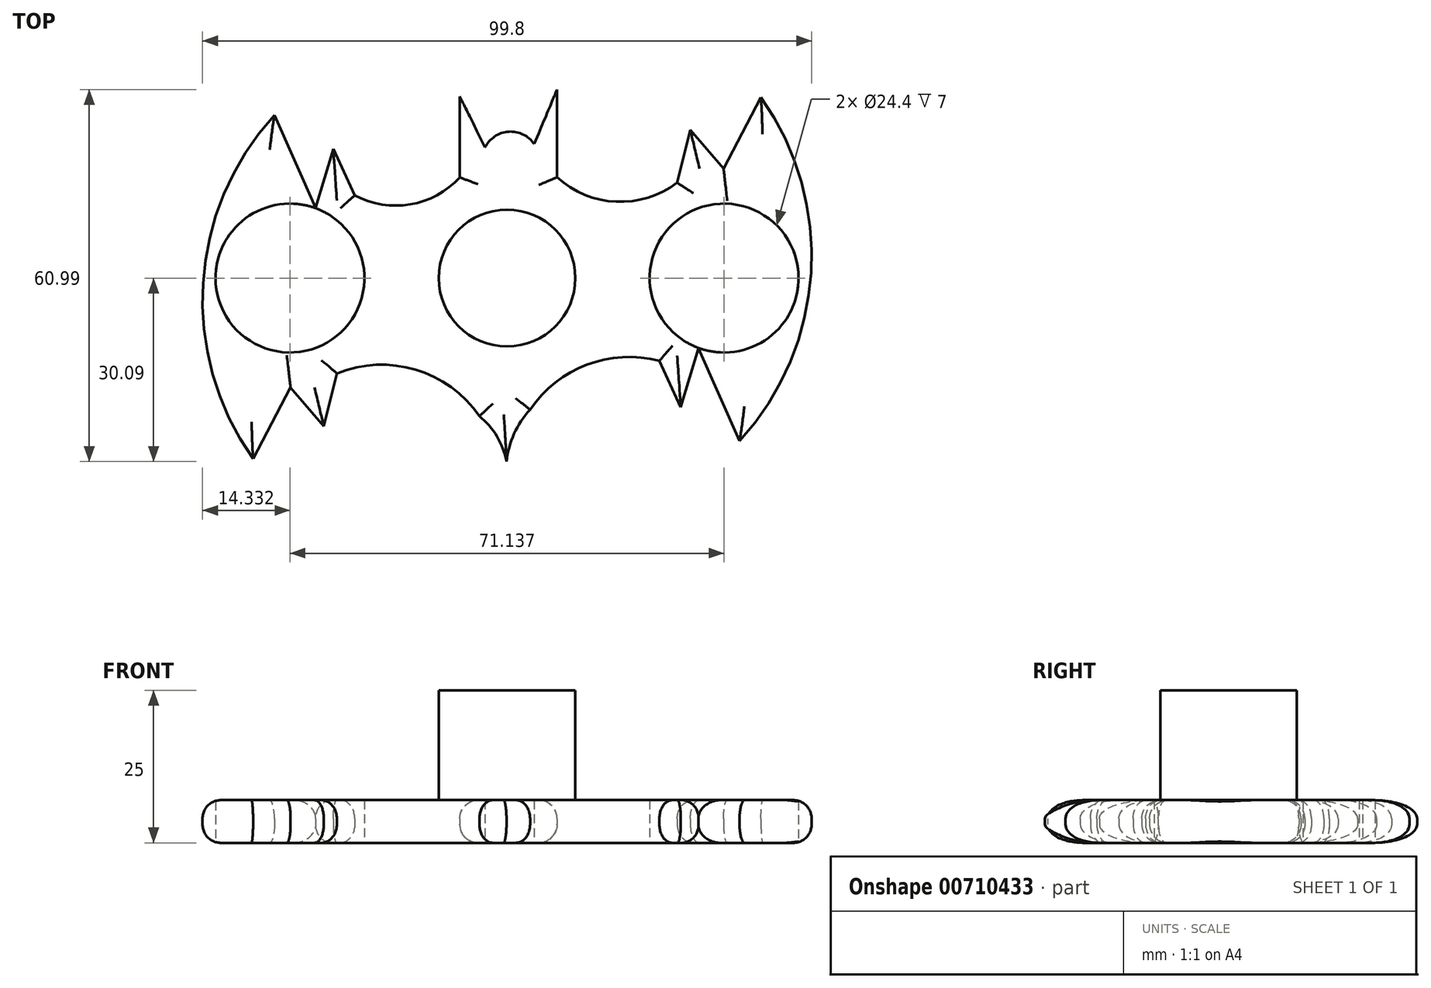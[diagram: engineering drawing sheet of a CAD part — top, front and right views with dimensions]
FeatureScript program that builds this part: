
annotation { "Feature Type Name" : "Feature", "Feature Type Description" : "" }
export const myFeature = defineFeature(function(context is Context, id is Id, definition is map)
    precondition{}
    {
        {
            var Q0;
            Q0=qCreatedBy(makeId("Top.planeOp"),FACE);
            var sketch = newSketch(context, id + "F0", { "sketchPlane" : qUnion([Q0])});
            skCircle(sketch, "E0", {"center": v(0, 0) * mm, "radius": 11.2 * mm});
            skCircle(sketch, "E1", {"center": v(0, 0) * mm, "radius": 13.2 * mm});
            skArc(sketch, "E2", {"start": v(-38.1, 26.72) * mm, "mid": v(-49.82, -0.84) * mm, "end": v(-41.61, -29.64) * mm});
            skArc(sketch, "E3.1.0", {"start": v(38.1, -26.72) * mm, "mid": v(49.82, 0.84) * mm, "end": v(41.61, 29.64) * mm});
            skLineSegment(sketch, "E4", {"start": v(-41.61, -29.64) * mm, "end": v(-35.48, -17.96) * mm});
            skLineSegment(sketch, "E5", {"start": v(-35.48, -17.96) * mm, "end": v(-35.48, -24.97) * mm});
            skArc(sketch, "E6", {"start": v(-4.53, -22.63) * mm, "mid": v(-14.98, -15.03) * mm, "end": v(-27.89, -15.62) * mm});
            skLineSegment(sketch, "E7.1.0", {"start": v(41.61, 29.64) * mm, "end": v(35.48, 17.96) * mm});
            skLineSegment(sketch, "E7.1.1", {"start": v(35.48, 17.96) * mm, "end": v(30.03, 24.29) * mm});
            skLineSegment(sketch, "E7.1.2", {"start": v(30.03, 24.29) * mm, "end": v(27.89, 15.62) * mm});
            skLineSegment(sketch, "E8", {"start": v(38.1, -26.72) * mm, "end": v(31.4, -11.53) * mm});
            skLineSegment(sketch, "E9", {"start": v(31.4, -11.53) * mm, "end": v(28.47, -21.17) * mm});
            skLineSegment(sketch, "E10", {"start": v(28.47, -21.17) * mm, "end": v(24.97, -13.58) * mm});
            skArc(sketch, "E11.1.0", {"start": v(-24.97, 13.58) * mm, "mid": v(-15.85, 12.08) * mm, "end": v(-7.74, 16.5) * mm});
            skLineSegment(sketch, "E11.1.2", {"start": v(-28.47, 21.17) * mm, "end": v(-24.97, 13.58) * mm});
            skLineSegment(sketch, "E11.1.4", {"start": v(-31.4, 11.53) * mm, "end": v(-28.47, 21.17) * mm});
            skLineSegment(sketch, "E11.1.5", {"start": v(-38.1, 26.72) * mm, "end": v(-31.4, 11.53) * mm});
            skArc(sketch, "E12", {"start": v(0, -34.06) * mm, "mid": v(-0.76, -27.75) * mm, "end": v(-4.53, -22.63) * mm});
            skArc(sketch, "E13.1.0", {"start": v(8.2, 16.53) * mm, "mid": v(17.88, 12.52) * mm, "end": v(27.89, 15.62) * mm});
            skLineSegment(sketch, "E14", {"start": v(-7.74, 16.5) * mm, "end": v(-7.74, 29.75) * mm});
            skLineSegment(sketch, "E15", {"start": v(-7.74, 29.75) * mm, "end": v(-3.6, 21.41) * mm});
            skLineSegment(sketch, "E16", {"start": v(8.2, 16.53) * mm, "end": v(8.2, 30.9) * mm});
            skLineSegment(sketch, "E17", {"start": v(8.2, 30.9) * mm, "end": v(4.45, 21.97) * mm});
            skArc(sketch, "E18", {"start": v(4.45, 21.97) * mm, "mid": v(0.27, 24) * mm, "end": v(-3.6, 21.41) * mm});
            skArc(sketch, "E19", {"start": v(24.97, -13.58) * mm, "mid": v(13.1, -14.2) * mm, "end": v(3.78, -21.57) * mm});
            skArc(sketch, "E20", {"start": v(3.78, -21.57) * mm, "mid": v(0.47, -27.38) * mm, "end": v(0, -34.06) * mm});
            skLineSegment(sketch, "E21.1.0", {"start": v(-35.48, -17.96) * mm, "end": v(-30.03, -24.29) * mm});
            skLineSegment(sketch, "E21.1.1", {"start": v(-30.03, -24.29) * mm, "end": v(-27.89, -15.62) * mm});
            skCircle(sketch, "E22", {"center": v(35.57, 0) * mm, "radius": 12.2 * mm});
            skCircle(sketch, "E23", {"center": v(-35.57, 0) * mm, "radius": 12.2 * mm});
            skSolve(sketch);
        }
        {
            var Q0;
            Q0=makeQuery(id+"F0.imprint","IMPRINT",FACE,{"disambiguationData":[TD([[makeQuery(id+"F0.imprint","IMPRINT",EDGE,{"derivedFrom":sQuery(id+"F0.wireOp",EDGE,"E0")}),-1.0]])]});
            var Q1;
            Q1=makeQuery(id+"F0.imprint","IMPRINT",FACE,{"disambiguationData":[TD([[makeQuery(id+"F0.imprint","IMPRINT",EDGE,{"derivedFrom":sQuery(id+"F0.wireOp",EDGE,"E1")}),-1.0]])]});
            extrude(context, id + "F1", {"entities" : qUnion([Q0, Q1]), "depth" : 7 * mm, "offsetDistance" : 25 * mm});
        }
        {
            var Q0;
            Q0=makeQuery(id+"F1.opExtrude","CAP_EDGE",EDGE,{"disambiguationData":[OSD([sQuery(id+"F0.wireOp",EDGE,"E20")])],"isStart":false});
            var Q1;
            Q1=makeQuery(id+"F1.opExtrude","CAP_EDGE",EDGE,{"disambiguationData":[OSD([sQuery(id+"F0.wireOp",EDGE,"E19")])],"isStart":false});
            var Q2;
            Q2=makeQuery(id+"F1.opExtrude","CAP_EDGE",EDGE,{"disambiguationData":[OSD([sQuery(id+"F0.wireOp",EDGE,"E9")])],"isStart":false});
            var Q3;
            Q3=makeQuery(id+"F1.opExtrude","CAP_EDGE",EDGE,{"disambiguationData":[OSD([sQuery(id+"F0.wireOp",EDGE,"E3.1.0")])],"isStart":false});
            var Q4;
            Q4=makeQuery(id+"F1.opExtrude","CAP_EDGE",EDGE,{"disambiguationData":[OSD([sQuery(id+"F0.wireOp",EDGE,"E8")])],"isStart":false});
            var Q5;
            Q5=makeQuery(id+"F1.opExtrude","CAP_EDGE",EDGE,{"disambiguationData":[OSD([sQuery(id+"F0.wireOp",EDGE,"E7.1.0")])],"isStart":false});
            var Q6;
            Q6=makeQuery(id+"F1.opExtrude","CAP_EDGE",EDGE,{"disambiguationData":[OSD([sQuery(id+"F0.wireOp",EDGE,"E7.1.1")])],"isStart":false});
            var Q7;
            Q7=makeQuery(id+"F1.opExtrude","CAP_EDGE",EDGE,{"disambiguationData":[OSD([sQuery(id+"F0.wireOp",EDGE,"E7.1.2")])],"isStart":false});
            var Q8;
            Q8=makeQuery(id+"F1.opExtrude","CAP_EDGE",EDGE,{"disambiguationData":[OSD([sQuery(id+"F0.wireOp",EDGE,"E13.1.0")])],"isStart":false});
            var Q9;
            Q9=makeQuery(id+"F1.opExtrude","CAP_EDGE",EDGE,{"disambiguationData":[OSD([sQuery(id+"F0.wireOp",EDGE,"E16")])],"isStart":false});
            var Q10;
            Q10=makeQuery(id+"F1.opExtrude","CAP_EDGE",EDGE,{"disambiguationData":[OSD([sQuery(id+"F0.wireOp",EDGE,"E14")])],"isStart":false});
            var Q11;
            Q11=makeQuery(id+"F1.opExtrude","CAP_EDGE",EDGE,{"disambiguationData":[OSD([sQuery(id+"F0.wireOp",EDGE,"E11.1.0")])],"isStart":false});
            var Q12;
            Q12=makeQuery(id+"F1.opExtrude","CAP_EDGE",EDGE,{"disambiguationData":[OSD([sQuery(id+"F0.wireOp",EDGE,"E11.1.2")])],"isStart":false});
            var Q13;
            Q13=makeQuery(id+"F1.opExtrude","CAP_EDGE",EDGE,{"disambiguationData":[OSD([sQuery(id+"F0.wireOp",EDGE,"E11.1.5")])],"isStart":false});
            var Q14;
            Q14=makeQuery(id+"F1.opExtrude","CAP_EDGE",EDGE,{"disambiguationData":[OSD([sQuery(id+"F0.wireOp",EDGE,"E11.1.4")])],"isStart":false});
            var Q15;
            Q15=makeQuery(id+"F1.opExtrude","CAP_EDGE",EDGE,{"disambiguationData":[OSD([sQuery(id+"F0.wireOp",EDGE,"E2")])],"isStart":false});
            var Q16;
            Q16=makeQuery(id+"F1.opExtrude","CAP_EDGE",EDGE,{"disambiguationData":[OSD([sQuery(id+"F0.wireOp",EDGE,"E4")])],"isStart":false});
            var Q17;
            Q17=makeQuery(id+"F1.opExtrude","CAP_EDGE",EDGE,{"disambiguationData":[OSD([sQuery(id+"F0.wireOp",EDGE,"wEF84jsq-XExs-cQrN-D3yr-Ib7uIkRzdJAm")])],"isStart":false});
            var Q18;
            Q18=makeQuery(id+"F1.opExtrude","CAP_EDGE",EDGE,{"disambiguationData":[OSD([sQuery(id+"F0.wireOp",EDGE,"E12")])],"isStart":false});
            var Q19;
            Q19=makeQuery(id+"F1.opExtrude","CAP_EDGE",EDGE,{"disambiguationData":[OSD([sQuery(id+"F0.wireOp",EDGE,"E5")])],"isStart":false});
            var Q20;
            Q20=makeQuery(id+"F1.opExtrude","CAP_EDGE",EDGE,{"disambiguationData":[OSD([sQuery(id+"F0.wireOp",EDGE,"E10")])],"isStart":false});
            var Q21;
            Q21=makeQuery(id+"F1.opExtrude","CAP_EDGE",EDGE,{"disambiguationData":[OSD([sQuery(id+"F0.wireOp",EDGE,"E21.1.1")])],"isStart":false});
            var Q22;
            Q22=makeQuery(id+"F1.opExtrude","CAP_EDGE",EDGE,{"disambiguationData":[OSD([sQuery(id+"F0.wireOp",EDGE,"E6")])],"isStart":false});
            var Q23;
            Q23=makeQuery(id+"F1.opExtrude","CAP_EDGE",EDGE,{"disambiguationData":[OSD([sQuery(id+"F0.wireOp",EDGE,"E21.1.0")])],"isStart":false});
            var Q24;
            Q24=makeQuery(id+"F1.opExtrude","CAP_EDGE",EDGE,{"disambiguationData":[OSD([sQuery(id+"F0.wireOp",EDGE,"E3.1.0")])],"isStart":true});
            var Q25;
            Q25=makeQuery(id+"F1.opExtrude","CAP_EDGE",EDGE,{"disambiguationData":[OSD([sQuery(id+"F0.wireOp",EDGE,"E8")])],"isStart":true});
            var Q26;
            Q26=makeQuery(id+"F1.opExtrude","CAP_EDGE",EDGE,{"disambiguationData":[OSD([sQuery(id+"F0.wireOp",EDGE,"E9")])],"isStart":true});
            var Q27;
            Q27=makeQuery(id+"F1.opExtrude","CAP_EDGE",EDGE,{"disambiguationData":[OSD([sQuery(id+"F0.wireOp",EDGE,"E10")])],"isStart":true});
            var Q28;
            Q28=makeQuery(id+"F1.opExtrude","CAP_EDGE",EDGE,{"disambiguationData":[OSD([sQuery(id+"F0.wireOp",EDGE,"E19")])],"isStart":true});
            var Q29;
            Q29=makeQuery(id+"F1.opExtrude","CAP_EDGE",EDGE,{"disambiguationData":[OSD([sQuery(id+"F0.wireOp",EDGE,"E6")])],"isStart":true});
            var Q30;
            Q30=makeQuery(id+"F1.opExtrude","CAP_EDGE",EDGE,{"disambiguationData":[OSD([sQuery(id+"F0.wireOp",EDGE,"E12")])],"isStart":true});
            var Q31;
            Q31=makeQuery(id+"F1.opExtrude","CAP_EDGE",EDGE,{"disambiguationData":[OSD([sQuery(id+"F0.wireOp",EDGE,"E20")])],"isStart":true});
            var Q32;
            Q32=makeQuery(id+"F1.opExtrude","CAP_EDGE",EDGE,{"disambiguationData":[OSD([sQuery(id+"F0.wireOp",EDGE,"E21.1.1")])],"isStart":true});
            var Q33;
            Q33=makeQuery(id+"F1.opExtrude","CAP_EDGE",EDGE,{"disambiguationData":[OSD([sQuery(id+"F0.wireOp",EDGE,"E21.1.0")])],"isStart":true});
            var Q34;
            Q34=makeQuery(id+"F1.opExtrude","CAP_EDGE",EDGE,{"disambiguationData":[OSD([sQuery(id+"F0.wireOp",EDGE,"E4")])],"isStart":true});
            var Q35;
            Q35=makeQuery(id+"F1.opExtrude","CAP_EDGE",EDGE,{"disambiguationData":[OSD([sQuery(id+"F0.wireOp",EDGE,"E2")])],"isStart":true});
            var Q36;
            Q36=makeQuery(id+"F1.opExtrude","CAP_EDGE",EDGE,{"disambiguationData":[OSD([sQuery(id+"F0.wireOp",EDGE,"E11.1.5")])],"isStart":true});
            var Q37;
            Q37=makeQuery(id+"F1.opExtrude","CAP_EDGE",EDGE,{"disambiguationData":[OSD([sQuery(id+"F0.wireOp",EDGE,"E11.1.4")])],"isStart":true});
            var Q38;
            Q38=makeQuery(id+"F1.opExtrude","CAP_EDGE",EDGE,{"disambiguationData":[OSD([sQuery(id+"F0.wireOp",EDGE,"E14")])],"isStart":true});
            var Q39;
            Q39=makeQuery(id+"F1.opExtrude","CAP_EDGE",EDGE,{"disambiguationData":[OSD([sQuery(id+"F0.wireOp",EDGE,"E16")])],"isStart":true});
            var Q40;
            Q40=makeQuery(id+"F1.opExtrude","CAP_EDGE",EDGE,{"disambiguationData":[OSD([sQuery(id+"F0.wireOp",EDGE,"E13.1.0")])],"isStart":true});
            var Q41;
            Q41=makeQuery(id+"F1.opExtrude","CAP_EDGE",EDGE,{"disambiguationData":[OSD([sQuery(id+"F0.wireOp",EDGE,"E7.1.2")])],"isStart":true});
            var Q42;
            Q42=makeQuery(id+"F1.opExtrude","CAP_EDGE",EDGE,{"disambiguationData":[OSD([sQuery(id+"F0.wireOp",EDGE,"E7.1.1")])],"isStart":true});
            var Q43;
            Q43=makeQuery(id+"F1.opExtrude","CAP_EDGE",EDGE,{"disambiguationData":[OSD([sQuery(id+"F0.wireOp",EDGE,"E7.1.0")])],"isStart":true});
            var Q44;
            Q44=makeQuery(id+"F1.opExtrude","CAP_EDGE",EDGE,{"disambiguationData":[OSD([sQuery(id+"F0.wireOp",EDGE,"E11.1.0")])],"isStart":true});
            var Q45;
            Q45=makeQuery(id+"F1.opExtrude","CAP_EDGE",EDGE,{"disambiguationData":[OSD([sQuery(id+"F0.wireOp",EDGE,"E11.1.2")])],"isStart":true});
            fillet(context, id + "F2", {"entities" : qUnion([Q0, Q1, Q2, Q3, Q4, Q5, Q6, Q7, Q8, Q9, Q10, Q11, Q12, Q13, Q14, Q15, Q16, Q17, Q18, Q19, Q20, Q21, Q22, Q23, Q24, Q25, Q26, Q27, Q28, Q29, Q30, Q31, Q32, Q33, Q34, Q35, Q36, Q37, Q38, Q39, Q40, Q41, Q42, Q43, Q44, Q45]), "radius" : 3 * mm, "tangentPropagation" : true, "allowEdgeOverflow" : false});
        }
        {
            var Q0;
            Q0=qCreatedBy(makeId("Top.planeOp"),FACE);
            var sketch = newSketch(context, id + "F3", { "sketchPlane" : qUnion([Q0])});
            skCircle(sketch, "E24", {"center": v(0, 0) * mm, "radius": 11.2 * mm});
            skSolve(sketch);
        }
        {
            var Q0;
            Q0=qSketchRegion(id+"F3",true);
            extrude(context, id + "F4", {"entities" : qUnion([Q0]), "operationType" : NewBodyOperationType.ADD, "depth" : 25 * mm, "offsetDistance" : 25 * mm});
        }
    });
